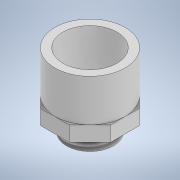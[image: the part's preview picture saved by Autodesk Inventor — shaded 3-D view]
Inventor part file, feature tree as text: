
AUTODESK INVENTOR PART (.ipt)
format: ipt  version: 2022 (Build 260153000, 153)  size: 166,912 bytes
history: native  units: mm
features: extrude x7, sketch x7, other x1, plane x1, thread x1
ambient origin geometry x8: Origin, YZ Plane, XZ Plane, XY Plane, X Axis, Y Axis, Z Axis, Center Point
bodies: Body1 (feature_tree)
feature tree (17):
  other  "Sólido1"
  extrude  "Extrusión1"  Depth=27.76mm
  extrude  "Extrusión2"  Depth=22.6mm
  plane  "Plano de trabajo2"
  extrude  "Extrusión4"  Depth=5.75mm
  extrude  "Extrusión5"  Depth=5.75mm
  extrude  "Extrusión6"  Depth=5.75mm
  extrude  "Extrusión7"  Depth=5.97mm TaperAngle=0.0deg
  thread  "Rosca2"  [1 undecoded]
  extrude  "Extrusión8"  Depth=18.97mm TaperAngle=0.0deg
  sketch  "Boceto1"  dims[d0=21.4mm d1=27.76mm]
  sketch  "Boceto2"  dims[d2=22.6mm d3=0.0mm d5=5.75mm]
  sketch  "Boceto4"  dims[d6=5.75mm d7=5.75mm]
  sketch  "Boceto5"  dims[d8=5.75mm d9=5.75mm]
  sketch  "Boceto6"  dims[d10=5.75mm d11=5.75mm]
  sketch  "Boceto7"  dims[d12=5.75mm d13=5.97mm d14=0.0mm d17=-18.5mm]
  sketch  "Boceto9"  dims[d18=13.6mm d19=18.97mm d20=0.0mm d21=18.97mm d22=0.0mm d25=13.4mm d26=18.6mm d27=18.97mm d28=0.0mm d29=13.6mm d30=18.97mm d31=0.0mm d32=14.87mm d33=0.0mm d34=8.47mm d35=0.0mm]
note: 1 required parameter value undecoded (feature->parameter linkage not recoverable at this tier; creation-order binding heuristic only, values carry confidence <= 0.55)
